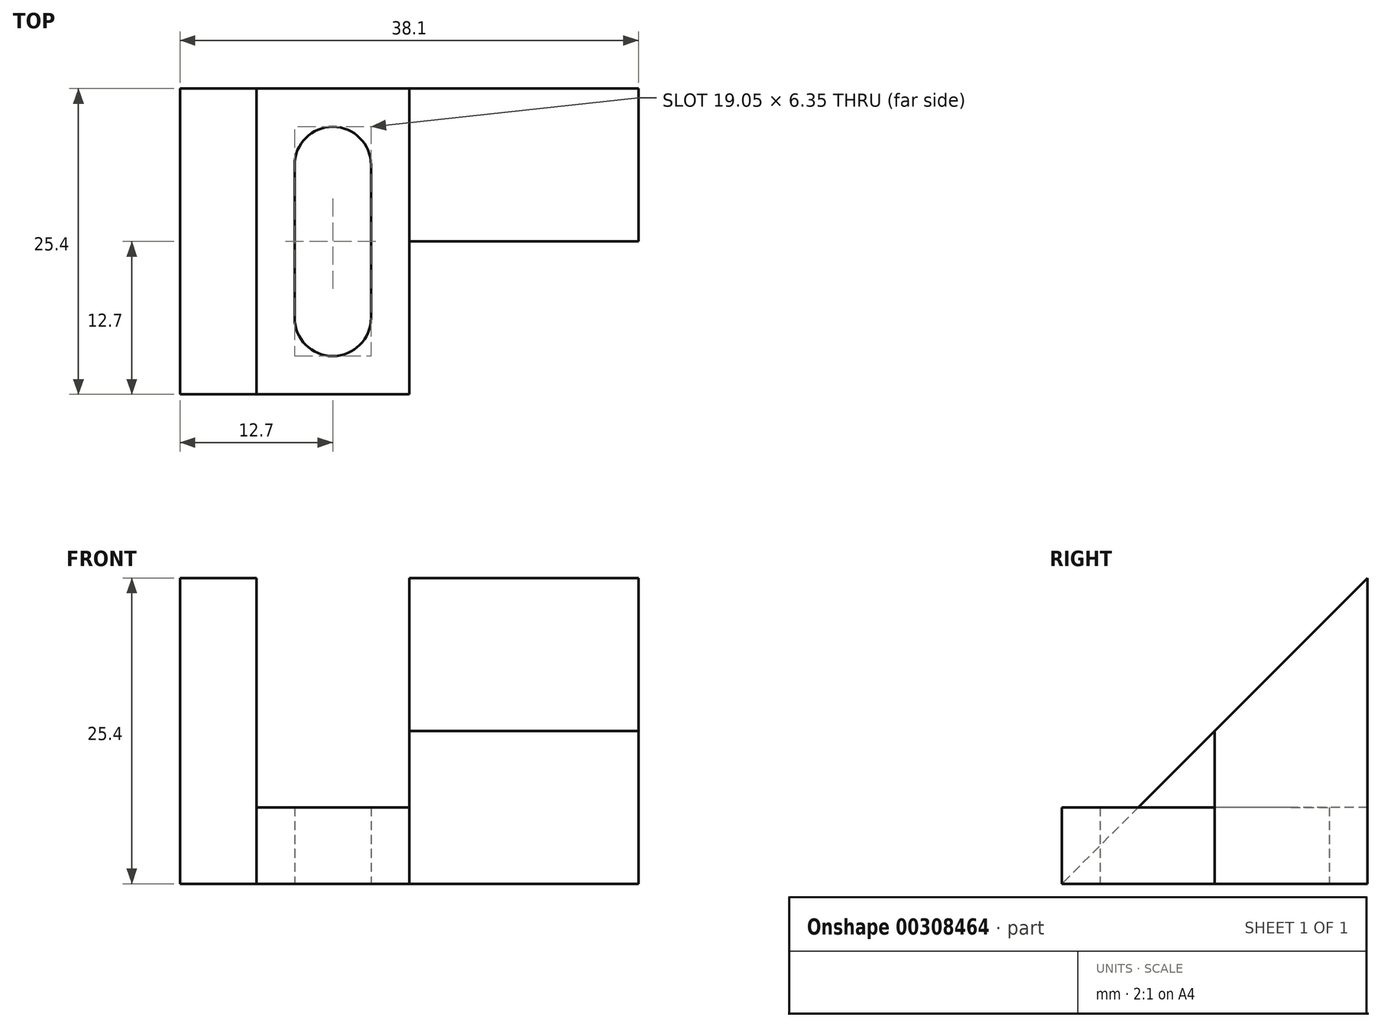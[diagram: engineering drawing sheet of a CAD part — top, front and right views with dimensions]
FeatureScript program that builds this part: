
annotation { "Feature Type Name" : "Feature", "Feature Type Description" : "" }
export const myFeature = defineFeature(function(context is Context, id is Id, definition is map)
    precondition{}
    {
        {
            var Q0;
            Q0=qCreatedBy(makeId("Top.planeOp"),FACE);
            var sketch = newSketch(context, id + "F0", { "sketchPlane" : qUnion([Q0])});
            skLineSegment(sketch, "E0.bottom", {"start": v(0, 0) * mm, "end": v(12.7, 0) * mm});
            skLineSegment(sketch, "E0.top", {"start": v(0, -25.4) * mm, "end": v(12.7, -25.4) * mm});
            skLineSegment(sketch, "E0.left", {"start": v(0, 0) * mm, "end": v(0, -25.4) * mm});
            skLineSegment(sketch, "E0.right", {"start": v(12.7, 0) * mm, "end": v(12.7, -25.4) * mm});
            skPoint(sketch, "E1.startSnap0", {"position": v(6.35, 0) * mm});
            skLineSegment(sketch, "E2", {"start": v(6.35, -6.35) * mm, "end": v(6.35, -19.05) * mm, "construction": true});
            skArc(sketch, "E3.0.startCap", {"start": v(3.18, -6.35) * mm, "mid": v(6.35, -3.18) * mm, "end": v(9.53, -6.35) * mm});
            skArc(sketch, "E3.0.endCap", {"start": v(9.53, -19.05) * mm, "mid": v(6.35, -22.23) * mm, "end": v(3.18, -19.05) * mm});
            skLineSegment(sketch, "E3.0.left", {"start": v(9.52, -6.35) * mm, "end": v(9.52, -19.05) * mm});
            skLineSegment(sketch, "E3.0.right", {"start": v(3.18, -6.35) * mm, "end": v(3.18, -19.05) * mm});
            skSolve(sketch);
        }
        {
            var Q0;
            Q0 = qSketchRegion(id + "F0", true);
            extrude(context, id + "F1", {"entities" : qUnion([Q0]), "depth" : 6.35 * mm});
        }
        {
            var Q0;
            Q0=makeQuery(id+"F1.opExtrude","SWEPT_FACE",FACE,{"disambiguationData":[OSD([sQuery(id+"F0.wireOp",EDGE,"E0.right")])]});
            var sketch = newSketch(context, id + "F2", { "sketchPlane" : qUnion([Q0])});
            skLineSegment(sketch, "E4", {"start": v(0, 0) * mm, "end": v(0, 25.4) * mm});
            skLineSegment(sketch, "E5", {"start": v(0, 25.4) * mm, "end": v(-12.7, 12.7) * mm});
            skLineSegment(sketch, "E6", {"start": v(-12.7, 12.7) * mm, "end": v(-12.7, 0) * mm});
            skLineSegment(sketch, "E7", {"start": v(-12.7, 0) * mm, "end": v(0, 0) * mm});
            skSolve(sketch);
        }
        {
            var Q0;
            Q0 = qSketchRegion(id + "F2", true);
            extrude(context, id + "F3", {"entities" : qUnion([Q0]), "operationType" : NewBodyOperationType.ADD, "depth" : 19.05 * mm});
        }
        {
            var Q0;
            Q0=makeQuery(id+"F1.opExtrude","SWEPT_FACE",FACE,{"disambiguationData":[OSD([sQuery(id+"F0.wireOp",EDGE,"E0.left")])]});
            var sketch = newSketch(context, id + "F4", { "sketchPlane" : qUnion([Q0])});
            skLineSegment(sketch, "E8", {"start": v(0, 0) * mm, "end": v(0, 25.4) * mm});
            skLineSegment(sketch, "E9", {"start": v(0, 25.4) * mm, "end": v(25.4, 0) * mm});
            skLineSegment(sketch, "E10", {"start": v(25.4, 0) * mm, "end": v(0, 0) * mm});
            skSolve(sketch);
        }
        {
            var Q0;
            Q0 = qSketchRegion(id + "F4", true);
            extrude(context, id + "F5", {"entities" : qUnion([Q0]), "operationType" : NewBodyOperationType.ADD, "depth" : 6.35 * mm});
        }
    });
